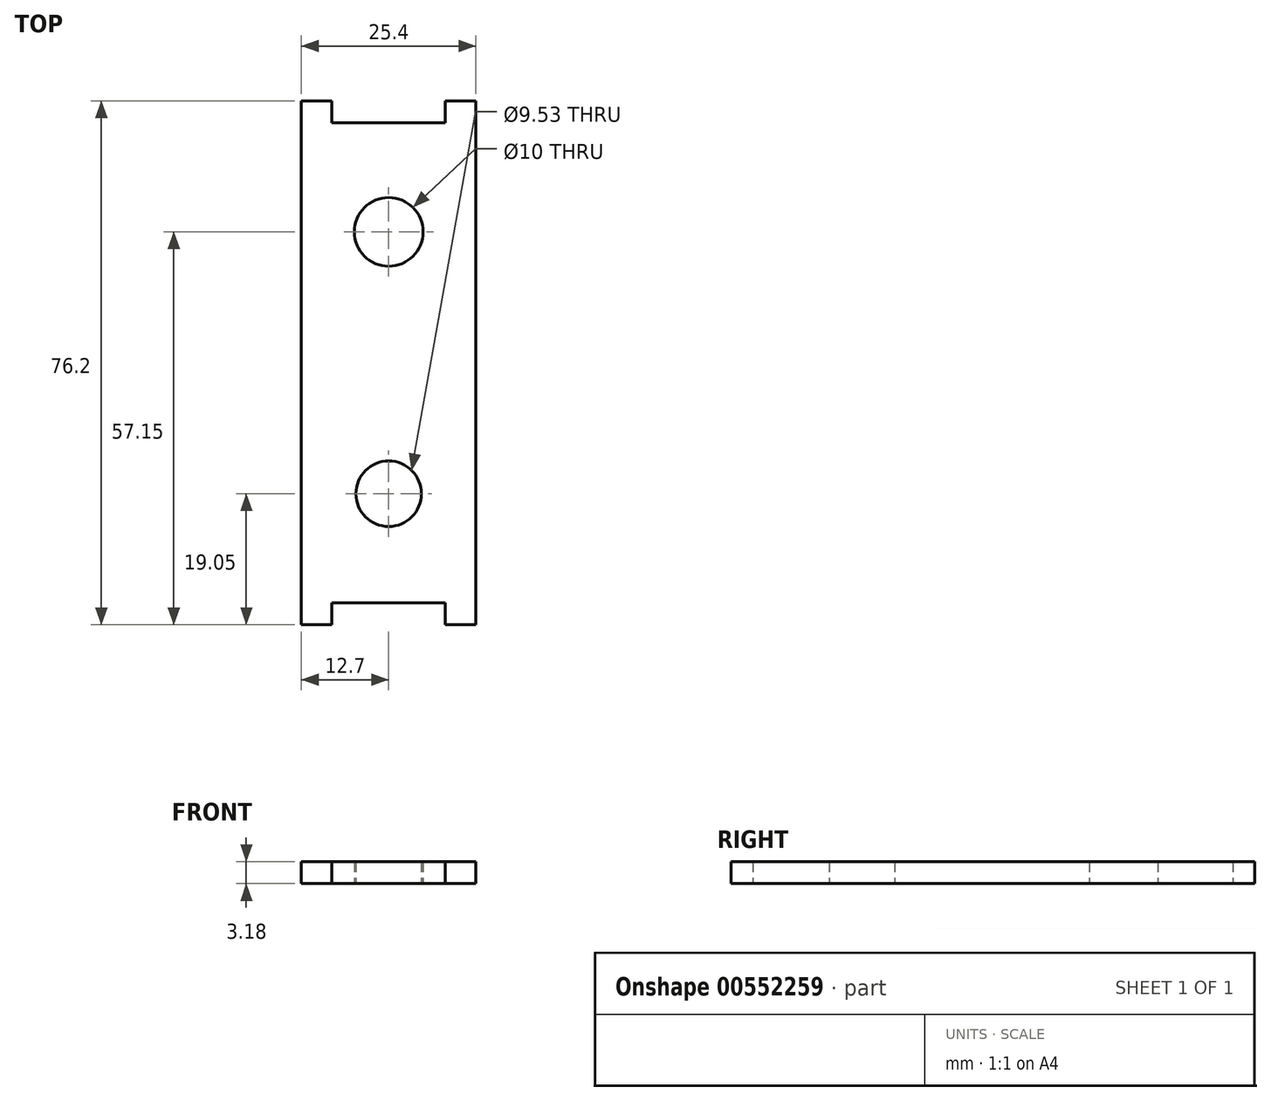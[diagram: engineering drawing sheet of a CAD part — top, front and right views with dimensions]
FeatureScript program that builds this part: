
annotation { "Feature Type Name" : "Feature", "Feature Type Description" : "" }
export const myFeature = defineFeature(function(context is Context, id is Id, definition is map)
    precondition{}
    {
        {
            var Q0;
            Q0=qCreatedBy(makeId("Top.planeOp"),FACE);
            var sketch = newSketch(context, id + "F0", { "sketchPlane" : qUnion([Q0])});
            skLineSegment(sketch, "E0.left", {"start": v(12.7, 38.1) * mm, "end": v(12.7, -38.1) * mm});
            skLineSegment(sketch, "E0.right", {"start": v(-12.7, 38.1) * mm, "end": v(-12.7, -38.1) * mm});
            skPoint(sketch, "E0.middle", {"position": v(0, 0) * mm});
            skLineSegment(sketch, "E1", {"start": v(-8.25, 38.1) * mm, "end": v(-8.25, 34.93) * mm});
            skLineSegment(sketch, "E2.top", {"start": v(8.26, 34.93) * mm, "end": v(-8.25, 34.93) * mm});
            skLineSegment(sketch, "E2.left", {"start": v(8.26, 38.1) * mm, "end": v(8.26, 34.93) * mm});
            skLineSegment(sketch, "E3", {"start": v(-12.7, 38.1) * mm, "end": v(-8.25, 38.1) * mm});
            skLineSegment(sketch, "E4", {"start": v(8.26, 38.1) * mm, "end": v(12.7, 38.1) * mm});
            skLineSegment(sketch, "E5", {"start": v(-8.26, -38.1) * mm, "end": v(-8.26, -34.93) * mm});
            skLineSegment(sketch, "E6.bottom", {"start": v(-8.26, -34.93) * mm, "end": v(8.26, -34.93) * mm});
            skLineSegment(sketch, "E6.left", {"start": v(-8.26, -34.93) * mm, "end": v(-8.26, -38.1) * mm});
            skLineSegment(sketch, "E6.right", {"start": v(8.26, -34.93) * mm, "end": v(8.26, -38.1) * mm});
            skLineSegment(sketch, "E7", {"start": v(-12.7, -38.1) * mm, "end": v(-8.26, -38.1) * mm});
            skLineSegment(sketch, "E8", {"start": v(8.26, -38.1) * mm, "end": v(12.7, -38.1) * mm});
            skCircle(sketch, "E9", {"center": v(0, -19.05) * mm, "radius": 4.76 * mm});
            skCircle(sketch, "E10", {"center": v(0, 19.05) * mm, "radius": 5 * mm});
            skSolve(sketch);
        }
        {
            var Q0;
            Q0 = qSketchRegion(id + "F0", true);
            extrude(context, id + "F1", {"entities" : qUnion([Q0]), "depth" : 3.17 * mm, "offsetDistance" : 25.4 * mm});
        }
    });
